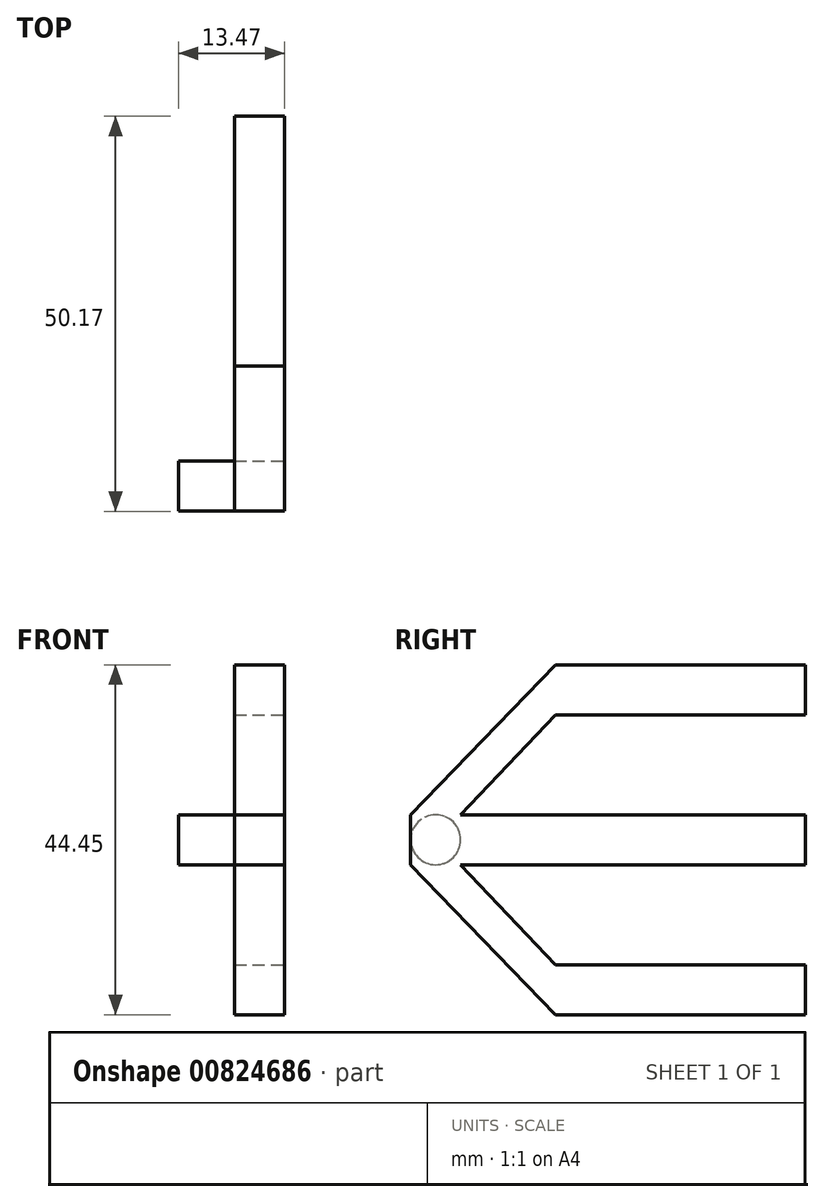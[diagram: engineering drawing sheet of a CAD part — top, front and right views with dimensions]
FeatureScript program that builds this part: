
annotation { "Feature Type Name" : "Feature", "Feature Type Description" : "" }
export const myFeature = defineFeature(function(context is Context, id is Id, definition is map)
    precondition{}
    {
        {
            var Q0;
            Q0=qCreatedBy(makeId("Front.planeOp"),FACE);
            var sketch = newSketch(context, id + "F0", { "sketchPlane" : qUnion([Q0])});
            skLineSegment(sketch, "E0.bottom", {"start": v(-30.17, -7.05) * mm, "end": v(-23.82, -7.05) * mm});
            skLineSegment(sketch, "E0.top", {"start": v(-30.17, -13.4) * mm, "end": v(-23.82, -13.4) * mm});
            skLineSegment(sketch, "E0.left", {"start": v(-30.17, -7.05) * mm, "end": v(-30.17, -13.4) * mm});
            skLineSegment(sketch, "E0.right", {"start": v(-23.82, -7.05) * mm, "end": v(-23.82, -13.4) * mm});
            skLineSegment(sketch, "E1", {"start": v(-30.17, -13.4) * mm, "end": v(-30.17, -26.1) * mm});
            skLineSegment(sketch, "E2", {"start": v(-30.17, -26.1) * mm, "end": v(-23.82, -26.1) * mm});
            skLineSegment(sketch, "E3", {"start": v(-23.82, -26.1) * mm, "end": v(-23.82, -13.4) * mm});
            skLineSegment(sketch, "E4", {"start": v(-30.17, -7.05) * mm, "end": v(-30.17, 5.65) * mm});
            skLineSegment(sketch, "E5", {"start": v(-30.17, 5.65) * mm, "end": v(-23.82, 5.65) * mm});
            skLineSegment(sketch, "E6", {"start": v(-23.82, 5.65) * mm, "end": v(-23.82, -7.05) * mm});
            skLineSegment(sketch, "E7", {"start": v(-30.17, -26.1) * mm, "end": v(-30.17, -32.45) * mm});
            skLineSegment(sketch, "E8", {"start": v(-30.17, -32.45) * mm, "end": v(-23.82, -32.45) * mm});
            skLineSegment(sketch, "E9", {"start": v(-23.82, -32.45) * mm, "end": v(-23.82, -26.1) * mm});
            skLineSegment(sketch, "E10", {"start": v(-30.17, 5.65) * mm, "end": v(-30.17, 12) * mm});
            skLineSegment(sketch, "E11", {"start": v(-30.17, 12) * mm, "end": v(-23.82, 12) * mm});
            skLineSegment(sketch, "E12", {"start": v(-23.82, 12) * mm, "end": v(-23.82, 5.65) * mm});
            skSolve(sketch);
        }
        {
            var Q0;
            Q0=makeQuery(id+"F0.imprint","IMPRINT",FACE,{"disambiguationData":[TD([[makeQuery(id+"F0.imprint","IMPRINT",EDGE,{"derivedFrom":sQuery(id+"F0.wireOp",EDGE,"E0.bottom")}),-1.0]])]});
            extrude(context, id + "F1", {"entities" : qUnion([Q0]), "depth" : 43.81 * mm, "offsetDistance" : 25.4 * mm});
        }
        {
            var Q0;
            Q0=makeQuery(id+"F0.imprint","IMPRINT",FACE,{"disambiguationData":[TD([[makeQuery(id+"F0.imprint","IMPRINT",EDGE,{"derivedFrom":sQuery(id+"F0.wireOp",EDGE,"E2")}),-1.0]])]});
            var Q1;
            Q1=makeQuery(id+"F0.imprint","IMPRINT",FACE,{"disambiguationData":[TD([[makeQuery(id+"F0.imprint","IMPRINT",EDGE,{"derivedFrom":sQuery(id+"F0.wireOp",EDGE,"E5")}),1.0]])]});
            extrude(context, id + "F2", {"entities" : qUnion([Q0, Q1]), "depth" : 25.4 * mm, "offsetDistance" : 25.4 * mm});
        }
        {
            var Q0;
            Q0=makeQuery(id+"F1.opExtrude","SWEPT_FACE",FACE,{"disambiguationData":[OSD([sQuery(id+"F0.wireOp",EDGE,"E0.top")])]});
            var sketch = newSketch(context, id + "F3", { "sketchPlane" : qUnion([Q0])});
            skLineSegment(sketch, "E13", {"start": v(-30.17, 43.82) * mm, "end": v(-30.17, 37.47) * mm});
            skLineSegment(sketch, "E14", {"start": v(-30.17, 37.47) * mm, "end": v(-23.82, 37.47) * mm});
            skLineSegment(sketch, "E15", {"start": v(-23.82, 37.47) * mm, "end": v(-23.82, 43.82) * mm});
            skLineSegment(sketch, "E16", {"start": v(-23.82, 43.82) * mm, "end": v(-30.17, 43.82) * mm});
            skSolve(sketch);
        }
        {
            var Q0;
            Q0=makeQuery(id+"F2.opExtrude","CAP_FACE",FACE,{"disambiguationData":[OSD([sQuery(id+"F0.wireOp",EDGE,"E2"),sQuery(id+"F0.wireOp",EDGE,"E7"),sQuery(id+"F0.wireOp",EDGE,"E8"),sQuery(id+"F0.wireOp",EDGE,"E9")])],"isStart":false});
            var sketch = newSketch(context, id + "F4", { "sketchPlane" : qUnion([Q0])});
            skLineSegment(sketch, "E17", {"start": v(-30.17, -26.1) * mm, "end": v(-23.82, -26.1) * mm});
            skLineSegment(sketch, "E18", {"start": v(-23.82, -26.1) * mm, "end": v(-23.82, -32.45) * mm});
            skLineSegment(sketch, "E19", {"start": v(-23.82, -32.45) * mm, "end": v(-30.17, -32.45) * mm});
            skLineSegment(sketch, "E20", {"start": v(-30.17, -32.45) * mm, "end": v(-30.17, -26.1) * mm});
            skSolve(sketch);
        }
        {
            var Q0;
            Q0=makeQuery(id+"F3.imprint","IMPRINT",FACE,{"disambiguationData":[TD([[makeQuery(id+"F3.imprint","IMPRINT",EDGE,{"derivedFrom":sQuery(id+"F3.wireOp",EDGE,"E13")}),1.0]])]});
            var Q1;
            Q1=makeQuery(id+"F4.imprint","IMPRINT",FACE,{"disambiguationData":[TD([[makeQuery(id+"F4.imprint","IMPRINT",EDGE,{"derivedFrom":sQuery(id+"F4.wireOp",EDGE,"E17")}),-1.0]])]});
            loft(context, id + "F5", {"sheetProfilesArray" : [{ "sheetProfileEntities" : qUnion([Q0]) }, { "sheetProfileEntities" : qUnion([Q1]) }]});
        }
        {
            var Q0;
            Q0=makeQuery(id+"F1.opExtrude","SWEPT_FACE",FACE,{"disambiguationData":[OSD([sQuery(id+"F0.wireOp",EDGE,"E0.bottom")])]});
            var sketch = newSketch(context, id + "F6", { "sketchPlane" : qUnion([Q0])});
            skLineSegment(sketch, "E21", {"start": v(-23.82, -43.82) * mm, "end": v(-30.17, -43.82) * mm});
            skLineSegment(sketch, "E22", {"start": v(-30.17, -43.82) * mm, "end": v(-30.17, -37.47) * mm});
            skLineSegment(sketch, "E23", {"start": v(-30.17, -37.47) * mm, "end": v(-23.82, -37.47) * mm});
            skLineSegment(sketch, "E24", {"start": v(-23.82, -37.47) * mm, "end": v(-23.82, -43.82) * mm});
            skSolve(sketch);
        }
        {
            var Q0;
            Q0=makeQuery(id+"F2.opExtrude","CAP_FACE",FACE,{"disambiguationData":[OSD([sQuery(id+"F0.wireOp",EDGE,"E5"),sQuery(id+"F0.wireOp",EDGE,"E10"),sQuery(id+"F0.wireOp",EDGE,"E11"),sQuery(id+"F0.wireOp",EDGE,"E12")])],"isStart":false});
            var sketch = newSketch(context, id + "F7", { "sketchPlane" : qUnion([Q0])});
            skLineSegment(sketch, "E25", {"start": v(-23.82, 5.65) * mm, "end": v(-30.17, 5.65) * mm});
            skLineSegment(sketch, "E26", {"start": v(-30.17, 5.65) * mm, "end": v(-30.17, 12) * mm});
            skLineSegment(sketch, "E27", {"start": v(-30.17, 12) * mm, "end": v(-23.82, 12) * mm});
            skLineSegment(sketch, "E28", {"start": v(-23.82, 12) * mm, "end": v(-23.82, 5.65) * mm});
            skSolve(sketch);
        }
        {
            var Q0;
            Q0=makeQuery(id+"F6.imprint","IMPRINT",FACE,{"disambiguationData":[TD([[makeQuery(id+"F6.imprint","IMPRINT",EDGE,{"derivedFrom":sQuery(id+"F6.wireOp",EDGE,"E21")}),1.0]])]});
            var Q1;
            Q1=makeQuery(id+"F7.imprint","IMPRINT",FACE,{"disambiguationData":[TD([[makeQuery(id+"F7.imprint","IMPRINT",EDGE,{"derivedFrom":sQuery(id+"F7.wireOp",EDGE,"E25")}),1.0]])]});
            loft(context, id + "F8", {"sheetProfilesArray" : [{ "sheetProfileEntities" : qUnion([Q0]) }, { "sheetProfileEntities" : qUnion([Q1]) }]});
        }
        {
            var Q0;
            Q0=makeQuery(id+"F1.opExtrude","SWEPT_BODY",BODY,{"disambiguationData":[OSD([sQuery(id+"F0.wireOp",EDGE,"E0.bottom"),sQuery(id+"F0.wireOp",EDGE,"E0.top"),sQuery(id+"F0.wireOp",EDGE,"E0.left"),sQuery(id+"F0.wireOp",EDGE,"E0.right")])]});
            var Q1;
            Q1=makeQuery(id+"F5.opLoft","SWEPT_BODY",BODY,{"disambiguationData":[OSD([makeQuery(id+"F3.imprint","IMPRINT",FACE,{"disambiguationData":[TD([[makeQuery(id+"F3.imprint","IMPRINT",EDGE,{"derivedFrom":sQuery(id+"F3.wireOp",EDGE,"E13")}),1.0]])]}),makeQuery(id+"F4.imprint","IMPRINT",FACE,{"disambiguationData":[TD([[makeQuery(id+"F4.imprint","IMPRINT",EDGE,{"derivedFrom":sQuery(id+"F4.wireOp",EDGE,"E17")}),-1.0]])]})])]});
            var Q2;
            Q2=makeQuery(id+"F2.opExtrude","SWEPT_BODY",BODY,{"disambiguationData":[OSD([sQuery(id+"F0.wireOp",EDGE,"E5"),sQuery(id+"F0.wireOp",EDGE,"E10"),sQuery(id+"F0.wireOp",EDGE,"E11"),sQuery(id+"F0.wireOp",EDGE,"E12")])]});
            var Q3;
            Q3=makeQuery(id+"F2.opExtrude","SWEPT_BODY",BODY,{"disambiguationData":[OSD([sQuery(id+"F0.wireOp",EDGE,"E2"),sQuery(id+"F0.wireOp",EDGE,"E7"),sQuery(id+"F0.wireOp",EDGE,"E8"),sQuery(id+"F0.wireOp",EDGE,"E9")])]});
            var Q4;
            Q4=makeQuery(id+"F8.opLoft","SWEPT_BODY",BODY,{"disambiguationData":[OSD([makeQuery(id+"F6.imprint","IMPRINT",FACE,{"disambiguationData":[TD([[makeQuery(id+"F6.imprint","IMPRINT",EDGE,{"derivedFrom":sQuery(id+"F6.wireOp",EDGE,"E21")}),1.0]])]}),makeQuery(id+"F7.imprint","IMPRINT",FACE,{"disambiguationData":[TD([[makeQuery(id+"F7.imprint","IMPRINT",EDGE,{"derivedFrom":sQuery(id+"F7.wireOp",EDGE,"E25")}),1.0]])]})])]});
            booleanBodies(context, id + "F9", {"operationType" : BooleanOperationType.UNION, "tools" : qUnion([Q0, Q1, Q2, Q3, Q4])});
        }
        {
            var Q0;
            {var subQ0=sQuery(id+"F0.wireOp",EDGE,"E0.left");Q0=makeQuery(id+"F9.opBoolean","MERGE",FACE,{"derivedFrom":[makeQuery(id+"F1.opExtrude","SWEPT_FACE",FACE,{"disambiguationData":[OSD([subQ0])]}),makeQuery(id+"F2.opExtrude","SWEPT_FACE",FACE,{"disambiguationData":[OSD([sQuery(id+"F0.wireOp",EDGE,"E7")])]}),makeQuery(id+"F2.opExtrude","SWEPT_FACE",FACE,{"disambiguationData":[OSD([sQuery(id+"F0.wireOp",EDGE,"E10")])]}),makeQuery(id+"F5.opLoft","SWEPT_FACE",FACE,{"disambiguationData":[OSD([sQuery(id+"F0.wireOp",EDGE,"E0.top"),subQ0,sQuery(id+"F0.wireOp",EDGE,"E1"),sQuery(id+"F3.wireOp",EDGE,"E13"),sQuery(id+"F3.wireOp",EDGE,"E14"),sQuery(id+"F3.wireOp",EDGE,"E16"),sQuery(id+"F4.wireOp",EDGE,"E17"),sQuery(id+"F4.wireOp",EDGE,"E19"),sQuery(id+"F4.wireOp",EDGE,"E20")])]}),makeQuery(id+"F8.opLoft","SWEPT_FACE",FACE,{"disambiguationData":[OSD([sQuery(id+"F0.wireOp",EDGE,"E0.bottom"),subQ0,sQuery(id+"F0.wireOp",EDGE,"E4"),sQuery(id+"F6.wireOp",EDGE,"E21"),sQuery(id+"F6.wireOp",EDGE,"E22"),sQuery(id+"F6.wireOp",EDGE,"E23"),sQuery(id+"F7.wireOp",EDGE,"E25"),sQuery(id+"F7.wireOp",EDGE,"E26"),sQuery(id+"F7.wireOp",EDGE,"E27")])]})]});}
            var sketch = newSketch(context, id + "F10", { "sketchPlane" : qUnion([Q0])});
            skLineSegment(sketch, "E29", {"start": v(43.82, -7.05) * mm, "end": v(37.47, -7.05) * mm});
            skLineSegment(sketch, "E30", {"start": v(37.47, -7.05) * mm, "end": v(37.47, -13.4) * mm});
            skLineSegment(sketch, "E31", {"start": v(37.47, -13.4) * mm, "end": v(43.82, -13.4) * mm});
            skLineSegment(sketch, "E32", {"start": v(43.82, -13.4) * mm, "end": v(43.82, -7.05) * mm});
            skCircle(sketch, "E33", {"center": v(40.64, -10.23) * mm, "radius": 3.18 * mm});
            skPoint(sketch, "E33.centerSnap0", {"position": v(43.82, -10.23) * mm});
            skPoint(sketch, "E33.centerSnap1", {"position": v(40.64, -7.05) * mm});
            skSolve(sketch);
        }
        {
            var Q0;
            {var subQ0=sQuery(id+"F10.wireOp",EDGE,"E33");var subQ1=makeQuery(id+"F10.imprint","INTERSECT",VERTEX,{"derivedFrom":[sQuery(id+"F10.wireOp",EDGE,"E32"),subQ0]});Q0=makeQuery(id+"F10.imprint","IMPRINT",FACE,{"disambiguationData":[TD([[makeQuery(id+"F10.imprint","IMPRINT",EDGE,{"disambiguationData":[TD([[subQ1,-1.0]])],"derivedFrom":subQ0}),1.0]])]});}
            extrude(context, id + "F11", {"entities" : qUnion([Q0]), "operationType" : NewBodyOperationType.ADD, "depth" : 7.11 * mm, "offsetDistance" : 25.4 * mm});
        }
        {
            var Q0;
            Q0=makeQuery(id+"F0.imprint","IMPRINT",FACE,{"disambiguationData":[TD([[makeQuery(id+"F0.imprint","IMPRINT",EDGE,{"derivedFrom":sQuery(id+"F0.wireOp",EDGE,"E5")}),1.0]])]});
            var Q1;
            Q1=makeQuery(id+"F0.imprint","IMPRINT",FACE,{"disambiguationData":[TD([[makeQuery(id+"F0.imprint","IMPRINT",EDGE,{"derivedFrom":sQuery(id+"F0.wireOp",EDGE,"E0.bottom")}),-1.0]])]});
            var Q2;
            Q2=makeQuery(id+"F0.imprint","IMPRINT",FACE,{"disambiguationData":[TD([[makeQuery(id+"F0.imprint","IMPRINT",EDGE,{"derivedFrom":sQuery(id+"F0.wireOp",EDGE,"E2")}),-1.0]])]});
            extrude(context, id + "F12", {"entities" : qUnion([Q0, Q1, Q2]), "operationType" : NewBodyOperationType.ADD, "oppositeDirection" : true, "depth" : 6.35 * mm, "offsetDistance" : 25.4 * mm});
        }
    });
